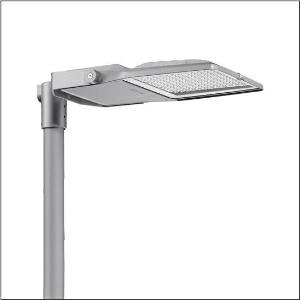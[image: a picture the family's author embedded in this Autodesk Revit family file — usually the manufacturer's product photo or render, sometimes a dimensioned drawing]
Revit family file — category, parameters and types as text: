
# Revit family: floodlight_fl_21_iq_midi___pl43_5xa7782f4a3a_c232
name_source: partatom
category: Lighting Fixtures
units: mm (PartAtom-declared; Revit-internal decimal feet)

## family parameters
Cut with Voids When Loaded = No
Host = Face
Light Source = No
Part Type = Normal
Room Calculation Point = No
Round Connector Dimension = Use Diameter
Shared = No

## types (1)
- --- (1 x LED, 38290 lm, 270.2 W, 4000K)
    Apparent Load = 270 VA
    CIE Flux Codes = 27 78 99 100 100
    Color Rendering = 70
    Color Temperature = 4000K
    Default Elevation = 1800 mm
    Description = Floodlight FL 21 iQ midi, floodlight, primary light control with lens, of PMMA, primary optical cover: protective disc, of toughened safety glass, transparent, light distribution: PL43, light emission: direct distribution, installation type: surface-mounted, LED, High Power LED, rated luminous flux: 38.290lm, luminous efficacy: 142lm/W, light colour: 740, colour temperature: 4000K, control gear: ECG iQ, control: optimised constant luminous flux control (CLO 2.0), Desk-Remote (wireless, voltage-free reading and setting of iQ features in the workshop via application-optimized NFC function/RFID function), Smart-Wire, Night-Set, Temp-Guard, Auto-Match, Street-Remote, with terminal, 6-pole, mains connection: 220..240V, AC, 50/60Hz, start of lifetime: 270W, end of service life: 287W, reduction: 118W, luminaire housing, of diecast aluminium, powder-coated, Siteco® metallic grey (DB 702S), corrosivity category C5 mid according to DIN EN ISO 12944, sealing non-destructively replaceable, please order mast flange separately, mast bracket, of steel, galvanised, powder-coated, Siteco® metallic grey (DB 702S), protection rating (complete): IP66, insulation class (complete): insulation class II (safety insulation), certification: CE, protection symbol: D, impact resistance: IK08, permissible operating ambient temperature: -40..+40°C, permissible operating ambient temperature for outdoor applications: -40..+50°C, standard: DIN EN 12944, LABS conformity tested according to VDMA 24364:2018-05, packaging unit: 1 piece

Light Distribution: PL43
    Height = 76 mm
    Lamp = 1 x LED
    Lamp Light Flux = 38290 lm
    Lamp Power = 270.2 W
    Lamp count = 1
    Length = 657 mm
    Luminous efficacy = 142 lm/W
    Manufacturer = Siteco
    ModVariant = No
    Model = 5XA7782F4A3A
    Number of Poles = 1
    OnlyDefault = Yes
    Power Factor = 1
    Product Name = Floodlight FL 21 iQ midi | PL43
    Product group = floodlight | pylon annexe
    ProductGroupID = 6200
    Protection Class = Protection class II
    Protection Degree = IP 66
    RLX_Detail_Level = 1
    RLX_Emergency_Light_Flux = 0 lm
    RLX_Emergency_Type = 0
    RLX_Emergency_Type_DB = No
    RlxData = <blob elided: 153633 chars, md5=83ac77bd>
    Socket = socket
    Standby Power = 0 W
    System Light Flux = 38290 lm
    System Power = 270 W
    Type Comments = factory setting: luminous flux: 100 % | dim-lin: 254 | 620 mA
    Type Image = l_1007123.jpg
    URL = http://relux.com
    VarID = @adj_052869
    Voltage = 0 V
    Weight = 0.00 kg
    Width = 442 mm

## geometry (parser evidence)
native form markers: Blend x4, Sweep x12
no freeform markers — native parametric forms only
